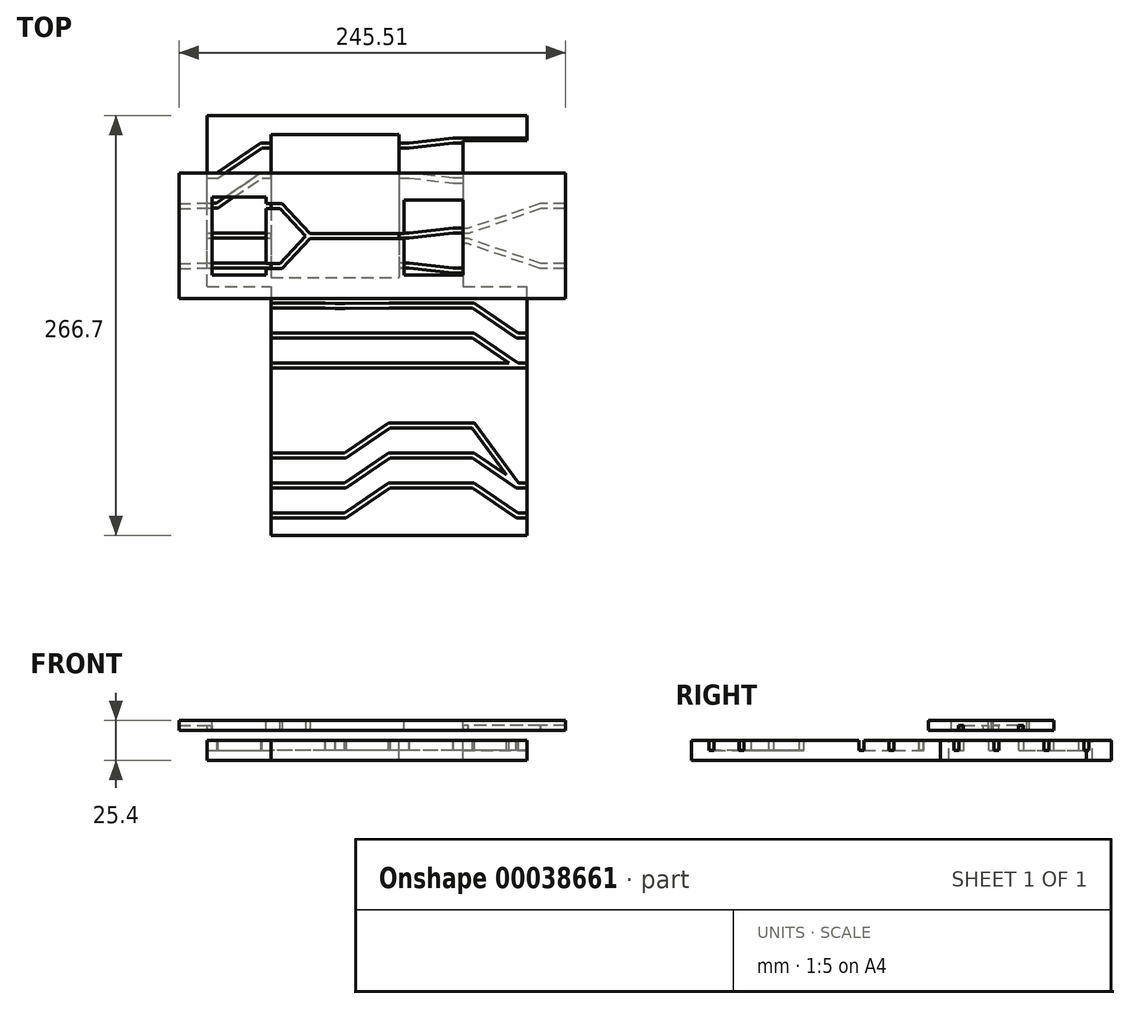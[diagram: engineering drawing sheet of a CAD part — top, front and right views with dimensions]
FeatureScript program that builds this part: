
annotation { "Feature Type Name" : "Feature", "Feature Type Description" : "" }
export const myFeature = defineFeature(function(context is Context, id is Id, definition is map)
    precondition{}
    {
        {
            var Q0;
            Q0=qCreatedBy(makeId("Top.planeOp"),FACE);
            var sketch = newSketch(context, id + "F0", { "sketchPlane" : qUnion([Q0])});
            skLineSegment(sketch, "E0.rect.bottom", {"start": v(-101.6, -133.35) * mm, "end": v(101.6, -133.35) * mm});
            skLineSegment(sketch, "E0.rect.top", {"start": v(-101.6, 133.35) * mm, "end": v(101.6, 133.35) * mm});
            skLineSegment(sketch, "E0.rect.left", {"start": v(-101.6, -133.35) * mm, "end": v(-101.6, 133.35) * mm});
            skLineSegment(sketch, "E0.rect.right", {"start": v(101.6, -133.35) * mm, "end": v(101.6, 133.35) * mm});
            skPoint(sketch, "E0.rect.middle", {"position": v(0, 0) * mm});
            skSolve(sketch);
        }
        {
            var Q0;
            Q0 = qSketchRegion(id + "F0", true);
            extrude(context, id + "F1", {"entities" : qUnion([Q0]), "depth" : 12.7 * mm});
        }
        {
            var Q0;
            Q0=makeQuery(id+"F1.opExtrude","CAP_FACE",FACE,{"disambiguationData":[OSD([sQuery(id+"F0.wireOp",EDGE,"E0.rect.bottom"),sQuery(id+"F0.wireOp",EDGE,"E0.rect.top"),sQuery(id+"F0.wireOp",EDGE,"E0.rect.left"),sQuery(id+"F0.wireOp",EDGE,"E0.rect.right")])],"isStart":false});
            var sketch = newSketch(context, id + "F2", { "sketchPlane" : qUnion([Q0])});
            skLineSegment(sketch, "E1", {"start": v(-101.6, 114.3) * mm, "end": v(101.6, 114.3) * mm, "construction": true});
            skLineSegment(sketch, "E2", {"start": v(-101.6, 95.25) * mm, "end": v(101.6, 95.25) * mm, "construction": true});
            skLineSegment(sketch, "E3", {"start": v(-101.6, 76.2) * mm, "end": v(101.6, 76.2) * mm, "construction": true});
            skLineSegment(sketch, "E4", {"start": v(-101.6, 57.15) * mm, "end": v(101.6, 57.15) * mm, "construction": true});
            skLineSegment(sketch, "E5", {"start": v(-101.6, 38.1) * mm, "end": v(101.6, 38.1) * mm, "construction": true});
            skLineSegment(sketch, "E6", {"start": v(-101.6, 12.69) * mm, "end": v(101.6, 12.69) * mm, "construction": true});
            skLineSegment(sketch, "E7", {"start": v(-101.6, -6.36) * mm, "end": v(101.6, -6.36) * mm, "construction": true});
            skLineSegment(sketch, "E8", {"start": v(-101.6, -25.41) * mm, "end": v(101.6, -25.41) * mm, "construction": true});
            skLineSegment(sketch, "E9", {"start": v(-101.6, -44.46) * mm, "end": v(101.6, -44.46) * mm, "construction": true});
            skLineSegment(sketch, "E10", {"start": v(-101.6, -63.51) * mm, "end": v(101.6, -63.51) * mm, "construction": true});
            skLineSegment(sketch, "E11", {"start": v(-101.6, -82.56) * mm, "end": v(101.6, -82.56) * mm, "construction": true});
            skLineSegment(sketch, "E12", {"start": v(-101.6, -101.61) * mm, "end": v(101.6, -101.61) * mm, "construction": true});
            skLineSegment(sketch, "E13", {"start": v(-101.6, -120.66) * mm, "end": v(101.6, -120.66) * mm, "construction": true});
            skLineSegment(sketch, "E14.0", {"start": v(-101.6, 133.35) * mm, "end": v(101.6, 133.35) * mm});
            skLineSegment(sketch, "E15.0", {"start": v(-101.6, -133.35) * mm, "end": v(-101.6, 133.35) * mm});
            skLineSegment(sketch, "E16.0", {"start": v(101.6, -133.35) * mm, "end": v(101.6, 133.35) * mm});
            skLineSegment(sketch, "E17.0", {"start": v(-101.6, -133.35) * mm, "end": v(101.6, -133.35) * mm});
            skLineSegment(sketch, "E18", {"start": v(-60.96, 133.35) * mm, "end": v(-60.96, -133.35) * mm, "construction": true});
            skLineSegment(sketch, "E19", {"start": v(-20.32, 133.35) * mm, "end": v(-20.32, -133.35) * mm, "construction": true});
            skLineSegment(sketch, "E20", {"start": v(20.32, -133.35) * mm, "end": v(20.32, 133.35) * mm, "construction": true});
            skLineSegment(sketch, "E21", {"start": v(60.96, 133.35) * mm, "end": v(60.96, -133.35) * mm, "construction": true});
            skLineSegment(sketch, "E22.0", {"start": v(-95.25, -133.35) * mm, "end": v(-95.25, 133.35) * mm, "construction": true});
            skLineSegment(sketch, "E23.0", {"start": v(-67.31, 133.35) * mm, "end": v(-67.31, -133.35) * mm, "construction": true});
            skLineSegment(sketch, "E24.0", {"start": v(-54.61, 133.35) * mm, "end": v(-54.61, -133.35) * mm, "construction": true});
            skLineSegment(sketch, "E25.0", {"start": v(-26.67, 133.35) * mm, "end": v(-26.67, -133.35) * mm, "construction": true});
            skLineSegment(sketch, "E26.0", {"start": v(-13.97, 133.35) * mm, "end": v(-13.97, -133.35) * mm, "construction": true});
            skLineSegment(sketch, "E27.0", {"start": v(26.67, -133.35) * mm, "end": v(26.67, 133.35) * mm, "construction": true});
            skLineSegment(sketch, "E28.0", {"start": v(13.97, -133.35) * mm, "end": v(13.97, 133.35) * mm, "construction": true});
            skLineSegment(sketch, "E29.0", {"start": v(54.6, 133.35) * mm, "end": v(54.6, -133.35) * mm, "construction": true});
            skLineSegment(sketch, "E30.0", {"start": v(67.3, 133.35) * mm, "end": v(67.3, -133.35) * mm, "construction": true});
            skLineSegment(sketch, "E31.0", {"start": v(95.25, -133.35) * mm, "end": v(95.25, 133.35) * mm, "construction": true});
            skLineSegment(sketch, "E32", {"start": v(-101.6, 95.25) * mm, "end": v(-95.25, 95.25) * mm});
            skLineSegment(sketch, "E33", {"start": v(-95.25, 95.25) * mm, "end": v(-67.31, 114.3) * mm});
            skLineSegment(sketch, "E34", {"start": v(-67.31, 114.3) * mm, "end": v(-60.96, 114.3) * mm});
            skLineSegment(sketch, "E35", {"start": v(-101.6, 76.2) * mm, "end": v(-95.25, 76.2) * mm});
            skLineSegment(sketch, "E36", {"start": v(-95.25, 76.2) * mm, "end": v(-67.31, 95.25) * mm});
            skLineSegment(sketch, "E37", {"start": v(-67.31, 95.25) * mm, "end": v(-60.96, 95.25) * mm});
            skLineSegment(sketch, "E38", {"start": v(-101.6, 57.15) * mm, "end": v(-95.25, 57.15) * mm});
            skLineSegment(sketch, "E39", {"start": v(-95.25, 57.15) * mm, "end": v(-67.31, 57.15) * mm});
            skLineSegment(sketch, "E40", {"start": v(-67.31, 57.15) * mm, "end": v(-60.96, 57.15) * mm});
            skLineSegment(sketch, "E41", {"start": v(-101.6, 38.1) * mm, "end": v(-95.25, 38.1) * mm});
            skLineSegment(sketch, "E42", {"start": v(-95.25, 38.1) * mm, "end": v(-67.31, 38.1) * mm});
            skLineSegment(sketch, "E43", {"start": v(-67.31, 38.1) * mm, "end": v(-60.96, 38.1) * mm});
            skLineSegment(sketch, "E44.bottom", {"start": v(-60.96, 121.3) * mm, "end": v(-20.32, 121.3) * mm});
            skLineSegment(sketch, "E44.top", {"start": v(-60.96, 30.34) * mm, "end": v(-20.32, 30.34) * mm});
            skLineSegment(sketch, "E44.left", {"start": v(-60.96, 121.3) * mm, "end": v(-60.96, 30.34) * mm});
            skLineSegment(sketch, "E44.right", {"start": v(-20.32, 121.3) * mm, "end": v(-20.32, 30.34) * mm});
            skLineSegment(sketch, "E45.bottom", {"start": v(60.96, 133.35) * mm, "end": v(101.6, 133.35) * mm});
            skLineSegment(sketch, "E45.top", {"start": v(60.96, 24.81) * mm, "end": v(101.6, 24.81) * mm});
            skLineSegment(sketch, "E45.left", {"start": v(60.96, 133.35) * mm, "end": v(60.96, 24.81) * mm});
            skLineSegment(sketch, "E45.right", {"start": v(101.6, 133.35) * mm, "end": v(101.6, 24.81) * mm});
            skLineSegment(sketch, "E46.bottom", {"start": v(-101.6, 24.81) * mm, "end": v(-60.96, 24.81) * mm});
            skLineSegment(sketch, "E46.top", {"start": v(-101.6, -133.35) * mm, "end": v(-60.96, -133.35) * mm});
            skLineSegment(sketch, "E46.left", {"start": v(-101.6, 24.81) * mm, "end": v(-101.6, -133.35) * mm});
            skLineSegment(sketch, "E46.right", {"start": v(-60.96, 24.81) * mm, "end": v(-60.96, -133.35) * mm});
            skLineSegment(sketch, "E47", {"start": v(-60.96, 12.69) * mm, "end": v(-54.61, 12.69) * mm});
            skLineSegment(sketch, "E48", {"start": v(-54.61, 12.69) * mm, "end": v(-26.67, 12.69) * mm});
            skLineSegment(sketch, "E49", {"start": v(-26.67, 12.69) * mm, "end": v(-20.47, 12.5) * mm});
            skLineSegment(sketch, "E50", {"start": v(-20.47, 12.5) * mm, "end": v(-13.97, 12.5) * mm});
            skLineSegment(sketch, "E51", {"start": v(-13.97, 12.5) * mm, "end": v(13.97, 12.69) * mm});
            skLineSegment(sketch, "E52", {"start": v(13.97, 12.69) * mm, "end": v(20.69, 12.68) * mm});
            skLineSegment(sketch, "E53", {"start": v(20.69, 12.68) * mm, "end": v(26.67, 12.68) * mm});
            skLineSegment(sketch, "E54", {"start": v(26.67, 12.68) * mm, "end": v(54.6, 12.68) * mm});
            skLineSegment(sketch, "E55", {"start": v(54.6, 12.68) * mm, "end": v(60.96, 12.68) * mm});
            skLineSegment(sketch, "E56", {"start": v(60.96, 12.68) * mm, "end": v(67.3, 12.68) * mm});
            skLineSegment(sketch, "E57", {"start": v(67.3, 12.68) * mm, "end": v(95.25, -6.36) * mm});
            skLineSegment(sketch, "E58", {"start": v(95.25, -6.36) * mm, "end": v(101.6, -6.36) * mm});
            skLineSegment(sketch, "E59", {"start": v(-60.96, -6.36) * mm, "end": v(-54.61, -6.36) * mm});
            skLineSegment(sketch, "E60", {"start": v(-54.61, -6.36) * mm, "end": v(-26.67, -6.36) * mm});
            skLineSegment(sketch, "E61", {"start": v(-26.67, -6.36) * mm, "end": v(-20.32, -6.36) * mm});
            skLineSegment(sketch, "E62", {"start": v(-20.32, -6.36) * mm, "end": v(-13.97, -6.36) * mm});
            skLineSegment(sketch, "E63", {"start": v(-13.97, -6.36) * mm, "end": v(13.97, -6.36) * mm});
            skLineSegment(sketch, "E64", {"start": v(13.97, -6.36) * mm, "end": v(20.32, -6.36) * mm});
            skLineSegment(sketch, "E65", {"start": v(20.32, -6.36) * mm, "end": v(26.67, -6.36) * mm});
            skLineSegment(sketch, "E66", {"start": v(26.67, -6.36) * mm, "end": v(54.6, -6.36) * mm});
            skLineSegment(sketch, "E67", {"start": v(54.6, -6.36) * mm, "end": v(60.96, -6.36) * mm});
            skLineSegment(sketch, "E68", {"start": v(60.96, -6.36) * mm, "end": v(67.3, -6.36) * mm});
            skLineSegment(sketch, "E69", {"start": v(67.3, -6.36) * mm, "end": v(95.25, -25.41) * mm});
            skLineSegment(sketch, "E70", {"start": v(95.25, -25.41) * mm, "end": v(101.6, -25.41) * mm});
            skLineSegment(sketch, "E71", {"start": v(-60.96, -25.41) * mm, "end": v(-54.61, -25.41) * mm});
            skLineSegment(sketch, "E72", {"start": v(-54.61, -25.41) * mm, "end": v(-26.67, -25.41) * mm});
            skLineSegment(sketch, "E73", {"start": v(-26.67, -25.41) * mm, "end": v(-20.32, -25.41) * mm});
            skLineSegment(sketch, "E74", {"start": v(-20.32, -25.41) * mm, "end": v(-13.97, -25.41) * mm});
            skLineSegment(sketch, "E75", {"start": v(-13.97, -25.41) * mm, "end": v(13.97, -25.41) * mm});
            skLineSegment(sketch, "E76", {"start": v(13.97, -25.41) * mm, "end": v(20.32, -25.41) * mm});
            skLineSegment(sketch, "E77", {"start": v(20.32, -25.41) * mm, "end": v(26.67, -25.41) * mm});
            skLineSegment(sketch, "E78", {"start": v(26.67, -25.41) * mm, "end": v(54.6, -25.41) * mm});
            skLineSegment(sketch, "E79", {"start": v(54.6, -25.41) * mm, "end": v(60.96, -25.41) * mm});
            skLineSegment(sketch, "E80", {"start": v(60.96, -25.41) * mm, "end": v(67.3, -25.41) * mm});
            skLineSegment(sketch, "E81", {"start": v(67.3, -25.41) * mm, "end": v(95.25, -25.41) * mm});
            skLineSegment(sketch, "E82", {"start": v(-60.96, -82.56) * mm, "end": v(-54.61, -82.56) * mm});
            skLineSegment(sketch, "E83", {"start": v(-54.61, -82.56) * mm, "end": v(-26.67, -82.56) * mm});
            skLineSegment(sketch, "E84", {"start": v(-26.67, -82.56) * mm, "end": v(-20.32, -82.56) * mm});
            skLineSegment(sketch, "E85", {"start": v(-20.32, -82.56) * mm, "end": v(-13.97, -82.56) * mm});
            skLineSegment(sketch, "E86", {"start": v(-13.97, -82.56) * mm, "end": v(13.97, -63.51) * mm});
            skLineSegment(sketch, "E87", {"start": v(13.97, -63.51) * mm, "end": v(20.32, -63.51) * mm});
            skLineSegment(sketch, "E88", {"start": v(20.32, -63.51) * mm, "end": v(26.67, -63.51) * mm});
            skLineSegment(sketch, "E89", {"start": v(26.67, -63.51) * mm, "end": v(54.6, -63.51) * mm});
            skLineSegment(sketch, "E90", {"start": v(54.6, -63.51) * mm, "end": v(60.96, -63.51) * mm});
            skLineSegment(sketch, "E91", {"start": v(60.96, -63.51) * mm, "end": v(67.3, -63.51) * mm});
            skLineSegment(sketch, "E92", {"start": v(67.3, -63.51) * mm, "end": v(95.25, -101.61) * mm});
            skLineSegment(sketch, "E93", {"start": v(95.25, -101.61) * mm, "end": v(101.6, -101.61) * mm});
            skLineSegment(sketch, "E94", {"start": v(-60.96, -101.61) * mm, "end": v(-54.61, -101.61) * mm});
            skLineSegment(sketch, "E95", {"start": v(-54.61, -101.61) * mm, "end": v(-26.67, -101.61) * mm});
            skLineSegment(sketch, "E96", {"start": v(-26.67, -101.61) * mm, "end": v(-20.32, -101.61) * mm});
            skLineSegment(sketch, "E97", {"start": v(-20.32, -101.61) * mm, "end": v(-13.97, -101.61) * mm});
            skLineSegment(sketch, "E98", {"start": v(-13.97, -101.61) * mm, "end": v(13.97, -82.56) * mm});
            skLineSegment(sketch, "E99", {"start": v(13.97, -82.56) * mm, "end": v(20.32, -82.56) * mm});
            skLineSegment(sketch, "E100", {"start": v(20.32, -82.56) * mm, "end": v(26.67, -82.56) * mm});
            skLineSegment(sketch, "E101", {"start": v(26.67, -82.56) * mm, "end": v(54.6, -82.56) * mm});
            skLineSegment(sketch, "E102", {"start": v(54.6, -82.56) * mm, "end": v(60.96, -82.56) * mm});
            skLineSegment(sketch, "E103", {"start": v(60.96, -82.56) * mm, "end": v(67.3, -82.56) * mm});
            skLineSegment(sketch, "E104", {"start": v(67.3, -82.56) * mm, "end": v(95.25, -101.61) * mm});
            skLineSegment(sketch, "E105", {"start": v(-60.96, -120.66) * mm, "end": v(-54.61, -120.66) * mm});
            skLineSegment(sketch, "E106", {"start": v(-54.61, -120.66) * mm, "end": v(-26.67, -120.66) * mm});
            skLineSegment(sketch, "E107", {"start": v(-26.67, -120.66) * mm, "end": v(-20.32, -120.66) * mm});
            skLineSegment(sketch, "E108", {"start": v(-20.32, -120.66) * mm, "end": v(-13.97, -120.66) * mm});
            skLineSegment(sketch, "E109", {"start": v(-13.97, -120.66) * mm, "end": v(13.97, -101.61) * mm});
            skLineSegment(sketch, "E110", {"start": v(13.97, -101.61) * mm, "end": v(20.32, -101.61) * mm});
            skLineSegment(sketch, "E111", {"start": v(20.32, -101.61) * mm, "end": v(26.67, -101.61) * mm});
            skLineSegment(sketch, "E112", {"start": v(26.67, -101.61) * mm, "end": v(54.6, -101.61) * mm});
            skLineSegment(sketch, "E113", {"start": v(54.6, -101.61) * mm, "end": v(60.96, -101.61) * mm});
            skLineSegment(sketch, "E114", {"start": v(60.96, -101.61) * mm, "end": v(67.3, -101.61) * mm});
            skLineSegment(sketch, "E115", {"start": v(67.3, -101.61) * mm, "end": v(95.25, -120.66) * mm});
            skLineSegment(sketch, "E116", {"start": v(95.25, -120.66) * mm, "end": v(101.6, -120.66) * mm});
            skLineSegment(sketch, "E117.0", {"start": v(-101.6, 117.47) * mm, "end": v(101.6, 117.48) * mm, "construction": true});
            skLineSegment(sketch, "E118.0", {"start": v(-101.6, 92.07) * mm, "end": v(101.6, 92.08) * mm, "construction": true});
            skLineSegment(sketch, "E119.0", {"start": v(-101.6, 60.32) * mm, "end": v(101.6, 60.33) * mm, "construction": true});
            skLineSegment(sketch, "E120", {"start": v(20.32, 114.3) * mm, "end": v(26.67, 114.3) * mm});
            skLineSegment(sketch, "E121", {"start": v(26.67, 114.3) * mm, "end": v(54.6, 117.48) * mm});
            skLineSegment(sketch, "E122", {"start": v(54.6, 117.48) * mm, "end": v(60.96, 117.48) * mm});
            skLineSegment(sketch, "E123", {"start": v(20.32, 95.25) * mm, "end": v(26.67, 95.25) * mm});
            skLineSegment(sketch, "E124", {"start": v(26.67, 95.25) * mm, "end": v(54.6, 92.08) * mm});
            skLineSegment(sketch, "E125", {"start": v(54.6, 92.08) * mm, "end": v(60.96, 92.08) * mm});
            skLineSegment(sketch, "E126.0", {"start": v(-101.6, 34.92) * mm, "end": v(101.6, 34.93) * mm, "construction": true});
            skLineSegment(sketch, "E127", {"start": v(20.32, 57.15) * mm, "end": v(26.67, 57.15) * mm});
            skLineSegment(sketch, "E128", {"start": v(26.67, 57.15) * mm, "end": v(54.6, 60.32) * mm});
            skLineSegment(sketch, "E129", {"start": v(54.6, 60.32) * mm, "end": v(60.96, 60.32) * mm});
            skLineSegment(sketch, "E130", {"start": v(20.32, 38.1) * mm, "end": v(26.67, 38.1) * mm});
            skLineSegment(sketch, "E131", {"start": v(26.67, 38.1) * mm, "end": v(54.6, 34.93) * mm});
            skLineSegment(sketch, "E132", {"start": v(54.6, 34.92) * mm, "end": v(60.96, 34.93) * mm});
            skLineSegment(sketch, "E133", {"start": v(60.96, 117.48) * mm, "end": v(67.3, 117.48) * mm});
            skLineSegment(sketch, "E134", {"start": v(67.3, 117.48) * mm, "end": v(95.25, 117.48) * mm});
            skLineSegment(sketch, "E135", {"start": v(95.25, 117.48) * mm, "end": v(101.6, 117.48) * mm});
            skLineSegment(sketch, "E136", {"start": v(60.96, 92.08) * mm, "end": v(67.3, 92.08) * mm});
            skLineSegment(sketch, "E137", {"start": v(67.3, 92.08) * mm, "end": v(95.25, 92.08) * mm});
            skLineSegment(sketch, "E138", {"start": v(95.25, 92.08) * mm, "end": v(101.6, 92.08) * mm});
            skLineSegment(sketch, "E139", {"start": v(60.96, 60.32) * mm, "end": v(67.3, 60.32) * mm});
            skLineSegment(sketch, "E140", {"start": v(67.3, 60.32) * mm, "end": v(95.25, 60.32) * mm});
            skLineSegment(sketch, "E141", {"start": v(95.25, 60.33) * mm, "end": v(101.6, 60.33) * mm});
            skLineSegment(sketch, "E142", {"start": v(60.96, 34.93) * mm, "end": v(67.3, 34.93) * mm});
            skLineSegment(sketch, "E143", {"start": v(67.3, 34.93) * mm, "end": v(95.25, 34.93) * mm});
            skLineSegment(sketch, "E144", {"start": v(95.25, 34.93) * mm, "end": v(101.6, 34.93) * mm});
            skLineSegment(sketch, "E145.bottom", {"start": v(-20.32, 121.3) * mm, "end": v(20.32, 121.3) * mm});
            skLineSegment(sketch, "E145.top", {"start": v(-20.32, 30.34) * mm, "end": v(20.32, 30.34) * mm});
            skLineSegment(sketch, "E145.right", {"start": v(20.32, 121.3) * mm, "end": v(20.32, 30.34) * mm});
            skSolve(sketch);
        }
        {
            var Q0;
            {var subQ4=sQuery(id+"F2.wireOp",EDGE,"E44.bottom");Q0=makeQuery(id+"F2.imprint","IMPRINT",FACE,{"disambiguationData":[TD([[makeQuery(id+"F2.imprint","IMPRINT",EDGE,{"derivedFrom":subQ4}),-1.0]])]});}
            var Q1;
            {var subQ6=sQuery(id+"F2.wireOp",EDGE,"E46.bottom");Q1=makeQuery(id+"F2.imprint","IMPRINT",FACE,{"disambiguationData":[TD([[makeQuery(id+"F2.imprint","IMPRINT",EDGE,{"derivedFrom":subQ6}),-1.0]])]});}
            var Q2;
            Q2=makeQuery(id+"F2.imprint","IMPRINT",FACE,{"disambiguationData":[TD([[makeQuery(id+"F2.imprint","IMPRINT",EDGE,{"derivedFrom":sQuery(id+"F2.wireOp",EDGE,"E45.bottom")}),-1.0]])]});
            var Q3;
            {var subQ4=sQuery(id+"F2.wireOp",EDGE,"E133");Q3=makeQuery(id+"F2.imprint","IMPRINT",FACE,{"disambiguationData":[TD([[makeQuery(id+"F2.imprint","IMPRINT",EDGE,{"derivedFrom":subQ4}),-1.0]])]});}
            var Q4;
            {var subQ5=sQuery(id+"F2.wireOp",EDGE,"E136");Q4=makeQuery(id+"F2.imprint","IMPRINT",FACE,{"disambiguationData":[TD([[makeQuery(id+"F2.imprint","IMPRINT",EDGE,{"derivedFrom":subQ5}),-1.0]])]});}
            var Q5;
            {var subQ4=sQuery(id+"F2.wireOp",EDGE,"E139");Q5=makeQuery(id+"F2.imprint","IMPRINT",FACE,{"disambiguationData":[TD([[makeQuery(id+"F2.imprint","IMPRINT",EDGE,{"derivedFrom":subQ4}),-1.0]])]});}
            var Q6;
            {var subQ1=sQuery(id+"F2.wireOp",EDGE,"E45.top");Q6=makeQuery(id+"F2.imprint","IMPRINT",FACE,{"disambiguationData":[TD([[makeQuery(id+"F2.imprint","IMPRINT",EDGE,{"derivedFrom":subQ1}),1.0]])]});}
            var Q7;
            {var subQ6=sQuery(id+"F2.wireOp",EDGE,"E145.bottom");Q7=makeQuery(id+"F2.imprint","IMPRINT",FACE,{"disambiguationData":[TD([[makeQuery(id+"F2.imprint","IMPRINT",EDGE,{"derivedFrom":subQ6}),-1.0]])]});}
            extrude(context, id + "F3", {"entities" : qUnion([Q0, Q1, Q2, Q3, Q4, Q5, Q6, Q7]), "operationType" : NewBodyOperationType.REMOVE, "oppositeDirection" : true, "depth" : 25.4 * mm});
        }
        {
            var Q0;
            Q0=makeQuery(id+"F1.opExtrude","SWEPT_FACE",FACE,{"disambiguationData":[OSD([sQuery(id+"F0.wireOp",EDGE,"E0.rect.right")])]});
            var sketch = newSketch(context, id + "F4", { "sketchPlane" : qUnion([Q0])});
            skPoint(sketch, "E146.0", {"position": v(-120.66, 12.7) * mm});
            skPoint(sketch, "E147.0", {"position": v(-101.61, 12.7) * mm});
            skPoint(sketch, "E148.0", {"position": v(-25.41, 12.7) * mm});
            skPoint(sketch, "E149.0", {"position": v(-6.36, 12.7) * mm});
            skPoint(sketch, "E150.0", {"position": v(34.92, 12.7) * mm});
            skPoint(sketch, "E151.0", {"position": v(60.32, 12.7) * mm});
            skPoint(sketch, "E152.0", {"position": v(92.08, 12.7) * mm});
            skPoint(sketch, "E153.0", {"position": v(117.48, 12.7) * mm});
            skLineSegment(sketch, "E154", {"start": v(-133.35, 6.35) * mm, "end": v(123.8, 6.35) * mm, "construction": true});
            skLineSegment(sketch, "E155.rect.bottom", {"start": v(-119.08, 6.35) * mm, "end": v(-122.25, 6.35) * mm});
            skLineSegment(sketch, "E155.rect.top", {"start": v(-119.08, 19.05) * mm, "end": v(-122.25, 19.05) * mm});
            skLineSegment(sketch, "E155.rect.left", {"start": v(-119.08, 6.35) * mm, "end": v(-119.08, 19.05) * mm});
            skLineSegment(sketch, "E155.rect.right", {"start": v(-122.25, 6.35) * mm, "end": v(-122.25, 19.05) * mm});
            skLineSegment(sketch, "E156.rect.bottom", {"start": v(-100.03, 6.35) * mm, "end": v(-103.2, 6.35) * mm});
            skLineSegment(sketch, "E156.rect.top", {"start": v(-100.03, 19.05) * mm, "end": v(-103.2, 19.05) * mm});
            skLineSegment(sketch, "E156.rect.left", {"start": v(-100.03, 6.35) * mm, "end": v(-100.03, 19.05) * mm});
            skLineSegment(sketch, "E156.rect.right", {"start": v(-103.2, 6.35) * mm, "end": v(-103.2, 19.05) * mm});
            skLineSegment(sketch, "E157.rect.bottom", {"start": v(-23.83, 6.35) * mm, "end": v(-27, 6.35) * mm});
            skLineSegment(sketch, "E157.rect.top", {"start": v(-23.83, 19.05) * mm, "end": v(-27, 19.05) * mm});
            skLineSegment(sketch, "E157.rect.left", {"start": v(-23.83, 6.35) * mm, "end": v(-23.83, 19.05) * mm});
            skLineSegment(sketch, "E157.rect.right", {"start": v(-27, 6.35) * mm, "end": v(-27, 19.05) * mm});
            skLineSegment(sketch, "E158.rect.bottom", {"start": v(-4.78, 6.35) * mm, "end": v(-7.95, 6.35) * mm});
            skLineSegment(sketch, "E158.rect.top", {"start": v(-4.78, 19.05) * mm, "end": v(-7.95, 19.05) * mm});
            skLineSegment(sketch, "E158.rect.left", {"start": v(-4.78, 6.35) * mm, "end": v(-4.78, 19.05) * mm});
            skLineSegment(sketch, "E158.rect.right", {"start": v(-7.95, 6.35) * mm, "end": v(-7.95, 19.05) * mm});
            skLineSegment(sketch, "E159.rect.bottom", {"start": v(36.51, 6.35) * mm, "end": v(33.34, 6.35) * mm});
            skLineSegment(sketch, "E159.rect.top", {"start": v(36.51, 19.05) * mm, "end": v(33.34, 19.05) * mm});
            skLineSegment(sketch, "E159.rect.left", {"start": v(36.51, 6.35) * mm, "end": v(36.51, 19.05) * mm});
            skLineSegment(sketch, "E159.rect.right", {"start": v(33.34, 6.35) * mm, "end": v(33.34, 19.05) * mm});
            skLineSegment(sketch, "E160.rect.bottom", {"start": v(61.91, 6.35) * mm, "end": v(58.74, 6.35) * mm});
            skLineSegment(sketch, "E160.rect.top", {"start": v(61.91, 19.05) * mm, "end": v(58.74, 19.05) * mm});
            skLineSegment(sketch, "E160.rect.left", {"start": v(61.91, 6.35) * mm, "end": v(61.91, 19.05) * mm});
            skLineSegment(sketch, "E160.rect.right", {"start": v(58.74, 6.35) * mm, "end": v(58.74, 19.05) * mm});
            skLineSegment(sketch, "E161.rect.bottom", {"start": v(93.66, 6.35) * mm, "end": v(90.49, 6.35) * mm});
            skLineSegment(sketch, "E161.rect.top", {"start": v(93.66, 19.05) * mm, "end": v(90.49, 19.05) * mm});
            skLineSegment(sketch, "E161.rect.left", {"start": v(93.66, 6.35) * mm, "end": v(93.66, 19.05) * mm});
            skLineSegment(sketch, "E161.rect.right", {"start": v(90.49, 6.35) * mm, "end": v(90.49, 19.05) * mm});
            skLineSegment(sketch, "E162.rect.bottom", {"start": v(119.06, 6.35) * mm, "end": v(115.89, 6.35) * mm});
            skLineSegment(sketch, "E162.rect.top", {"start": v(119.06, 19.05) * mm, "end": v(115.89, 19.05) * mm});
            skLineSegment(sketch, "E162.rect.left", {"start": v(119.06, 6.35) * mm, "end": v(119.06, 19.05) * mm});
            skLineSegment(sketch, "E162.rect.right", {"start": v(115.89, 6.35) * mm, "end": v(115.89, 19.05) * mm});
            skSolve(sketch);
        }
        {
            var Q0;
            {var subQ5=sQuery(id+"F4.wireOp",EDGE,"E155.rect.bottom");Q0=makeQuery(id+"F4.imprint","IMPRINT",FACE,{"disambiguationData":[TD([[makeQuery(id+"F4.imprint","IMPRINT",EDGE,{"derivedFrom":subQ5}),-1.0]])]});}
            var Q1;
            Q1=sQuery(id+"F2.wireOp",EDGE,"E116");
            var Q2;
            Q2=sQuery(id+"F2.wireOp",EDGE,"E115");
            var Q3;
            Q3=sQuery(id+"F2.wireOp",EDGE,"E114");
            var Q4;
            Q4=sQuery(id+"F2.wireOp",EDGE,"E113");
            var Q5;
            Q5=sQuery(id+"F2.wireOp",EDGE,"E112");
            var Q6;
            Q6=sQuery(id+"F2.wireOp",EDGE,"E111");
            var Q7;
            Q7=sQuery(id+"F2.wireOp",EDGE,"E110");
            var Q8;
            Q8=sQuery(id+"F2.wireOp",EDGE,"E109");
            var Q9;
            Q9=sQuery(id+"F2.wireOp",EDGE,"E108");
            var Q10;
            Q10=sQuery(id+"F2.wireOp",EDGE,"E107");
            var Q11;
            Q11=sQuery(id+"F2.wireOp",EDGE,"E106");
            var Q12;
            Q12=sQuery(id+"F2.wireOp",EDGE,"E105");
            sweep(context, id + "F5", {"operationType" : NewBodyOperationType.REMOVE, "profiles" : qUnion([Q0]), "path" : qUnion([Q1, Q2, Q3, Q4, Q5, Q6, Q7, Q8, Q9, Q10, Q11, Q12])});
        }
        {
            var Q0;
            {var subQ5=sQuery(id+"F4.wireOp",EDGE,"E156.rect.bottom");Q0=makeQuery(id+"F4.imprint","IMPRINT",FACE,{"disambiguationData":[TD([[makeQuery(id+"F4.imprint","IMPRINT",EDGE,{"derivedFrom":subQ5}),-1.0]])]});}
            var Q1;
            Q1=sQuery(id+"F2.wireOp",EDGE,"E93");
            var Q2;
            Q2=sQuery(id+"F2.wireOp",EDGE,"E104");
            var Q3;
            Q3=sQuery(id+"F2.wireOp",EDGE,"E103");
            var Q4;
            Q4=sQuery(id+"F2.wireOp",EDGE,"E102");
            var Q5;
            Q5=sQuery(id+"F2.wireOp",EDGE,"E101");
            var Q6;
            Q6=sQuery(id+"F2.wireOp",EDGE,"E100");
            var Q7;
            Q7=sQuery(id+"F2.wireOp",EDGE,"E99");
            var Q8;
            Q8=sQuery(id+"F2.wireOp",EDGE,"E98");
            var Q9;
            Q9=sQuery(id+"F2.wireOp",EDGE,"E97");
            var Q10;
            Q10=sQuery(id+"F2.wireOp",EDGE,"E96");
            var Q11;
            Q11=sQuery(id+"F2.wireOp",EDGE,"E95");
            var Q12;
            Q12=sQuery(id+"F2.wireOp",EDGE,"E94");
            sweep(context, id + "F6", {"operationType" : NewBodyOperationType.REMOVE, "profiles" : qUnion([Q0]), "path" : qUnion([Q1, Q2, Q3, Q4, Q5, Q6, Q7, Q8, Q9, Q10, Q11, Q12])});
        }
        {
            var Q0;
            {var subQ5=sQuery(id+"F4.wireOp",EDGE,"E156.rect.bottom");Q0=makeQuery(id+"F4.imprint","IMPRINT",FACE,{"disambiguationData":[TD([[makeQuery(id+"F4.imprint","IMPRINT",EDGE,{"derivedFrom":subQ5}),-1.0]])]});}
            var Q1;
            Q1=sQuery(id+"F2.wireOp",EDGE,"E93");
            var Q2;
            Q2=sQuery(id+"F2.wireOp",EDGE,"E92");
            var Q3;
            Q3=sQuery(id+"F2.wireOp",EDGE,"E91");
            var Q4;
            Q4=sQuery(id+"F2.wireOp",EDGE,"E90");
            var Q5;
            Q5=sQuery(id+"F2.wireOp",EDGE,"E89");
            var Q6;
            Q6=sQuery(id+"F2.wireOp",EDGE,"E88");
            var Q7;
            Q7=sQuery(id+"F2.wireOp",EDGE,"E87");
            var Q8;
            Q8=sQuery(id+"F2.wireOp",EDGE,"E86");
            var Q9;
            Q9=sQuery(id+"F2.wireOp",EDGE,"E85");
            var Q10;
            Q10=sQuery(id+"F2.wireOp",EDGE,"E84");
            var Q11;
            Q11=sQuery(id+"F2.wireOp",EDGE,"E83");
            var Q12;
            Q12=sQuery(id+"F2.wireOp",EDGE,"E82");
            sweep(context, id + "F7", {"operationType" : NewBodyOperationType.REMOVE, "profiles" : qUnion([Q0]), "path" : qUnion([Q1, Q2, Q3, Q4, Q5, Q6, Q7, Q8, Q9, Q10, Q11, Q12])});
        }
        {
            var Q0;
            {var subQ5=sQuery(id+"F4.wireOp",EDGE,"E157.rect.bottom");Q0=makeQuery(id+"F4.imprint","IMPRINT",FACE,{"disambiguationData":[TD([[makeQuery(id+"F4.imprint","IMPRINT",EDGE,{"derivedFrom":subQ5}),-1.0]])]});}
            var Q1;
            Q1=sQuery(id+"F2.wireOp",EDGE,"E70");
            var Q2;
            Q2=sQuery(id+"F2.wireOp",EDGE,"E81");
            var Q3;
            Q3=sQuery(id+"F2.wireOp",EDGE,"E80");
            var Q4;
            Q4=sQuery(id+"F2.wireOp",EDGE,"E79");
            var Q5;
            Q5=sQuery(id+"F2.wireOp",EDGE,"E78");
            var Q6;
            Q6=sQuery(id+"F2.wireOp",EDGE,"E77");
            var Q7;
            Q7=sQuery(id+"F2.wireOp",EDGE,"E76");
            var Q8;
            Q8=sQuery(id+"F2.wireOp",EDGE,"E75");
            var Q9;
            Q9=sQuery(id+"F2.wireOp",EDGE,"E74");
            var Q10;
            Q10=sQuery(id+"F2.wireOp",EDGE,"E73");
            var Q11;
            Q11=sQuery(id+"F2.wireOp",EDGE,"E72");
            var Q12;
            Q12=sQuery(id+"F2.wireOp",EDGE,"E71");
            sweep(context, id + "F8", {"operationType" : NewBodyOperationType.REMOVE, "profiles" : qUnion([Q0]), "path" : qUnion([Q1, Q2, Q3, Q4, Q5, Q6, Q7, Q8, Q9, Q10, Q11, Q12])});
        }
        {
            var Q0;
            {var subQ5=sQuery(id+"F4.wireOp",EDGE,"E158.rect.bottom");Q0=makeQuery(id+"F4.imprint","IMPRINT",FACE,{"disambiguationData":[TD([[makeQuery(id+"F4.imprint","IMPRINT",EDGE,{"derivedFrom":subQ5}),-1.0]])]});}
            var Q1;
            Q1=sQuery(id+"F2.wireOp",EDGE,"E58");
            var Q2;
            Q2=sQuery(id+"F2.wireOp",EDGE,"E57");
            var Q3;
            Q3=sQuery(id+"F2.wireOp",EDGE,"E56");
            var Q4;
            Q4=sQuery(id+"F2.wireOp",EDGE,"E55");
            var Q5;
            Q5=sQuery(id+"F2.wireOp",EDGE,"E54");
            var Q6;
            Q6=sQuery(id+"F2.wireOp",EDGE,"E53");
            var Q7;
            Q7=sQuery(id+"F2.wireOp",EDGE,"E52");
            var Q8;
            Q8=sQuery(id+"F2.wireOp",EDGE,"E51");
            var Q9;
            Q9=sQuery(id+"F2.wireOp",EDGE,"E50");
            var Q10;
            Q10=sQuery(id+"F2.wireOp",EDGE,"E49");
            var Q11;
            Q11=sQuery(id+"F2.wireOp",EDGE,"E48");
            var Q12;
            Q12=sQuery(id+"F2.wireOp",EDGE,"E47");
            sweep(context, id + "F9", {"operationType" : NewBodyOperationType.REMOVE, "profiles" : qUnion([Q0]), "path" : qUnion([Q1, Q2, Q3, Q4, Q5, Q6, Q7, Q8, Q9, Q10, Q11, Q12])});
        }
        {
            var Q0;
            {var subQ5=sQuery(id+"F4.wireOp",EDGE,"E157.rect.bottom");Q0=makeQuery(id+"F4.imprint","IMPRINT",FACE,{"disambiguationData":[TD([[makeQuery(id+"F4.imprint","IMPRINT",EDGE,{"derivedFrom":subQ5}),-1.0]])]});}
            var Q1;
            Q1=sQuery(id+"F2.wireOp",EDGE,"E70");
            var Q2;
            Q2=sQuery(id+"F2.wireOp",EDGE,"E69");
            var Q3;
            Q3=sQuery(id+"F2.wireOp",EDGE,"E68");
            var Q4;
            Q4=sQuery(id+"F2.wireOp",EDGE,"E67");
            var Q5;
            Q5=sQuery(id+"F2.wireOp",EDGE,"E66");
            var Q6;
            Q6=sQuery(id+"F2.wireOp",EDGE,"E65");
            var Q7;
            Q7=sQuery(id+"F2.wireOp",EDGE,"E64");
            var Q8;
            Q8=sQuery(id+"F2.wireOp",EDGE,"E63");
            var Q9;
            Q9=sQuery(id+"F2.wireOp",EDGE,"E62");
            var Q10;
            Q10=sQuery(id+"F2.wireOp",EDGE,"E61");
            var Q11;
            Q11=sQuery(id+"F2.wireOp",EDGE,"E60");
            var Q12;
            Q12=sQuery(id+"F2.wireOp",EDGE,"E59");
            sweep(context, id + "F10", {"operationType" : NewBodyOperationType.REMOVE, "profiles" : qUnion([Q0]), "path" : qUnion([Q1, Q2, Q3, Q4, Q5, Q6, Q7, Q8, Q9, Q10, Q11, Q12])});
        }
        {
            var Q0;
            Q0=makeQuery(id+"F4.imprint","IMPRINT",FACE,{"disambiguationData":[TD([[makeQuery(id+"F4.imprint","IMPRINT",EDGE,{"derivedFrom":sQuery(id+"F4.wireOp",EDGE,"E159.rect.bottom")}),-1.0]])]});
            var Q1;
            Q1=sQuery(id+"F2.wireOp",EDGE,"E144");
            var Q2;
            Q2=sQuery(id+"F2.wireOp",EDGE,"E143");
            var Q3;
            Q3=sQuery(id+"F2.wireOp",EDGE,"E142");
            var Q4;
            Q4=sQuery(id+"F2.wireOp",EDGE,"E132");
            var Q5;
            Q5=sQuery(id+"F2.wireOp",EDGE,"E131");
            var Q6;
            Q6=sQuery(id+"F2.wireOp",EDGE,"E130");
            sweep(context, id + "F11", {"operationType" : NewBodyOperationType.REMOVE, "profiles" : qUnion([Q0]), "path" : qUnion([Q1, Q2, Q3, Q4, Q5, Q6])});
        }
        {
            var Q0;
            Q0=makeQuery(id+"F4.imprint","IMPRINT",FACE,{"disambiguationData":[TD([[makeQuery(id+"F4.imprint","IMPRINT",EDGE,{"derivedFrom":sQuery(id+"F4.wireOp",EDGE,"E160.rect.bottom")}),-1.0]])]});
            var Q1;
            Q1=sQuery(id+"F2.wireOp",EDGE,"E141");
            var Q2;
            Q2=sQuery(id+"F2.wireOp",EDGE,"E140");
            var Q3;
            Q3=sQuery(id+"F2.wireOp",EDGE,"E139");
            var Q4;
            Q4=sQuery(id+"F2.wireOp",EDGE,"E129");
            var Q5;
            Q5=sQuery(id+"F2.wireOp",EDGE,"E128");
            var Q6;
            Q6=sQuery(id+"F2.wireOp",EDGE,"E127");
            sweep(context, id + "F12", {"operationType" : NewBodyOperationType.REMOVE, "profiles" : qUnion([Q0]), "path" : qUnion([Q1, Q2, Q3, Q4, Q5, Q6])});
        }
        {
            var Q0;
            Q0=makeQuery(id+"F4.imprint","IMPRINT",FACE,{"disambiguationData":[TD([[makeQuery(id+"F4.imprint","IMPRINT",EDGE,{"derivedFrom":sQuery(id+"F4.wireOp",EDGE,"E161.rect.bottom")}),-1.0]])]});
            var Q1;
            Q1=sQuery(id+"F2.wireOp",EDGE,"E138");
            var Q2;
            Q2=sQuery(id+"F2.wireOp",EDGE,"E137");
            var Q3;
            Q3=sQuery(id+"F2.wireOp",EDGE,"E136");
            var Q4;
            Q4=sQuery(id+"F2.wireOp",EDGE,"E125");
            var Q5;
            Q5=sQuery(id+"F2.wireOp",EDGE,"E124");
            var Q6;
            Q6=sQuery(id+"F2.wireOp",EDGE,"E123");
            sweep(context, id + "F13", {"operationType" : NewBodyOperationType.REMOVE, "profiles" : qUnion([Q0]), "path" : qUnion([Q1, Q2, Q3, Q4, Q5, Q6])});
        }
        {
            var Q0;
            Q0=makeQuery(id+"F4.imprint","IMPRINT",FACE,{"disambiguationData":[TD([[makeQuery(id+"F4.imprint","IMPRINT",EDGE,{"derivedFrom":sQuery(id+"F4.wireOp",EDGE,"E162.rect.bottom")}),-1.0]])]});
            var Q1;
            Q1=sQuery(id+"F2.wireOp",EDGE,"E135");
            var Q2;
            Q2=sQuery(id+"F2.wireOp",EDGE,"E134");
            var Q3;
            Q3=sQuery(id+"F2.wireOp",EDGE,"E133");
            var Q4;
            Q4=sQuery(id+"F2.wireOp",EDGE,"E122");
            var Q5;
            Q5=sQuery(id+"F2.wireOp",EDGE,"E121");
            var Q6;
            Q6=sQuery(id+"F2.wireOp",EDGE,"E120");
            sweep(context, id + "F14", {"operationType" : NewBodyOperationType.REMOVE, "profiles" : qUnion([Q0]), "path" : qUnion([Q1, Q2, Q3, Q4, Q5, Q6])});
        }
        {
            var Q0;
            Q0=makeQuery(id+"F1.opExtrude","SWEPT_FACE",FACE,{"disambiguationData":[OSD([sQuery(id+"F0.wireOp",EDGE,"E0.rect.left")])]});
            var sketch = newSketch(context, id + "F15", { "sketchPlane" : qUnion([Q0])});
            skPoint(sketch, "E163.0", {"position": v(-95.25, 12.7) * mm});
            skPoint(sketch, "E164.0", {"position": v(-76.2, 12.7) * mm});
            skPoint(sketch, "E165.0", {"position": v(-57.15, 12.7) * mm});
            skPoint(sketch, "E166.0", {"position": v(-38.1, 12.7) * mm});
            skLineSegment(sketch, "E167", {"start": v(-133.35, 6.35) * mm, "end": v(-24.81, 6.35) * mm, "construction": true});
            skLineSegment(sketch, "E168.rect.bottom", {"start": v(-93.66, 6.35) * mm, "end": v(-96.84, 6.35) * mm});
            skLineSegment(sketch, "E168.rect.top", {"start": v(-93.66, 19.05) * mm, "end": v(-96.84, 19.05) * mm});
            skLineSegment(sketch, "E168.rect.left", {"start": v(-93.66, 6.35) * mm, "end": v(-93.66, 19.05) * mm});
            skLineSegment(sketch, "E168.rect.right", {"start": v(-96.84, 6.35) * mm, "end": v(-96.84, 19.05) * mm});
            skLineSegment(sketch, "E169.rect.bottom", {"start": v(-74.61, 6.35) * mm, "end": v(-77.79, 6.35) * mm});
            skLineSegment(sketch, "E169.rect.top", {"start": v(-74.61, 19.05) * mm, "end": v(-77.79, 19.05) * mm});
            skLineSegment(sketch, "E169.rect.left", {"start": v(-74.61, 6.35) * mm, "end": v(-74.61, 19.05) * mm});
            skLineSegment(sketch, "E169.rect.right", {"start": v(-77.79, 6.35) * mm, "end": v(-77.79, 19.05) * mm});
            skLineSegment(sketch, "E170.rect.bottom", {"start": v(-55.56, 6.35) * mm, "end": v(-58.74, 6.35) * mm});
            skLineSegment(sketch, "E170.rect.top", {"start": v(-55.56, 19.05) * mm, "end": v(-58.74, 19.05) * mm});
            skLineSegment(sketch, "E170.rect.left", {"start": v(-55.56, 6.35) * mm, "end": v(-55.56, 19.05) * mm});
            skLineSegment(sketch, "E170.rect.right", {"start": v(-58.74, 6.35) * mm, "end": v(-58.74, 19.05) * mm});
            skLineSegment(sketch, "E171.rect.bottom", {"start": v(-36.51, 6.35) * mm, "end": v(-39.69, 6.35) * mm});
            skLineSegment(sketch, "E171.rect.top", {"start": v(-36.51, 19.05) * mm, "end": v(-39.69, 19.05) * mm});
            skLineSegment(sketch, "E171.rect.left", {"start": v(-36.51, 6.35) * mm, "end": v(-36.51, 19.05) * mm});
            skLineSegment(sketch, "E171.rect.right", {"start": v(-39.69, 6.35) * mm, "end": v(-39.69, 19.05) * mm});
            skSolve(sketch);
        }
        {
            var Q0;
            {var subQ3=sQuery(id+"F15.wireOp",EDGE,"E168.rect.bottom");Q0=makeQuery(id+"F15.imprint","IMPRINT",FACE,{"disambiguationData":[TD([[makeQuery(id+"F15.imprint","IMPRINT",EDGE,{"derivedFrom":subQ3}),-1.0]])]});}
            var Q1;
            Q1=sQuery(id+"F2.wireOp",EDGE,"E32");
            var Q2;
            Q2=sQuery(id+"F2.wireOp",EDGE,"E34");
            var Q3;
            Q3=sQuery(id+"F2.wireOp",EDGE,"E33");
            sweep(context, id + "F16", {"operationType" : NewBodyOperationType.REMOVE, "profiles" : qUnion([Q0]), "path" : qUnion([Q1, Q2, Q3])});
        }
        {
            var Q0;
            {var subQ5=sQuery(id+"F15.wireOp",EDGE,"E169.rect.bottom");Q0=makeQuery(id+"F15.imprint","IMPRINT",FACE,{"disambiguationData":[TD([[makeQuery(id+"F15.imprint","IMPRINT",EDGE,{"derivedFrom":subQ5}),-1.0]])]});}
            var Q1;
            Q1=sQuery(id+"F2.wireOp",EDGE,"E35");
            var Q2;
            Q2=sQuery(id+"F2.wireOp",EDGE,"E36");
            var Q3;
            Q3=sQuery(id+"F2.wireOp",EDGE,"E37");
            sweep(context, id + "F17", {"operationType" : NewBodyOperationType.REMOVE, "profiles" : qUnion([Q0]), "path" : qUnion([Q1, Q2, Q3])});
        }
        {
            var Q0;
            {var subQ5=sQuery(id+"F15.wireOp",EDGE,"E170.rect.bottom");Q0=makeQuery(id+"F15.imprint","IMPRINT",FACE,{"disambiguationData":[TD([[makeQuery(id+"F15.imprint","IMPRINT",EDGE,{"derivedFrom":subQ5}),-1.0]])]});}
            var Q1;
            Q1=sQuery(id+"F2.wireOp",EDGE,"E38");
            var Q2;
            Q2=sQuery(id+"F2.wireOp",EDGE,"E39");
            var Q3;
            Q3=sQuery(id+"F2.wireOp",EDGE,"E40");
            sweep(context, id + "F18", {"operationType" : NewBodyOperationType.REMOVE, "profiles" : qUnion([Q0]), "path" : qUnion([Q1, Q2, Q3])});
        }
        {
            var Q0;
            {var subQ5=sQuery(id+"F15.wireOp",EDGE,"E171.rect.bottom");Q0=makeQuery(id+"F15.imprint","IMPRINT",FACE,{"disambiguationData":[TD([[makeQuery(id+"F15.imprint","IMPRINT",EDGE,{"derivedFrom":subQ5}),-1.0]])]});}
            var Q1;
            Q1=sQuery(id+"F2.wireOp",EDGE,"E41");
            var Q2;
            Q2=sQuery(id+"F2.wireOp",EDGE,"E42");
            var Q3;
            Q3=sQuery(id+"F2.wireOp",EDGE,"E43");
            sweep(context, id + "F19", {"operationType" : NewBodyOperationType.REMOVE, "profiles" : qUnion([Q0]), "path" : qUnion([Q1, Q2, Q3])});
        }
        {
            var Q0;
            Q0=qCreatedBy(makeId("Top.planeOp"),FACE);
            cPlane(context, id + "F20", {"entities" : qUnion([Q0]), "cplaneType" : CPlaneType.OFFSET, "offset" : 25.4 * mm, "width" : 152.4 * mm, "height" : 152.4 * mm});
        }
        {
            var Q0;
            Q0=qCreatedBy(id+"F20.planeOp",FACE);
            var sketch = newSketch(context, id + "F21", { "sketchPlane" : qUnion([Q0])});
            skLineSegment(sketch, "E172.bottom", {"start": v(-119.54, 96.78) * mm, "end": v(125.97, 96.78) * mm});
            skLineSegment(sketch, "E172.top", {"start": v(-119.54, 17.15) * mm, "end": v(125.97, 17.15) * mm});
            skLineSegment(sketch, "E172.left", {"start": v(-119.54, 96.78) * mm, "end": v(-119.54, 17.15) * mm});
            skLineSegment(sketch, "E172.right", {"start": v(125.97, 96.78) * mm, "end": v(125.97, 17.15) * mm});
            skSolve(sketch);
        }
        {
            var Q0;
            Q0=makeQuery(id+"F21.imprint","IMPRINT",FACE,{"disambiguationData":[TD([[makeQuery(id+"F21.imprint","IMPRINT",EDGE,{"derivedFrom":sQuery(id+"F21.wireOp",EDGE,"E172.bottom")}),-1.0]])]});
            extrude(context, id + "F22", {"entities" : qUnion([Q0]), "oppositeDirection" : true, "depth" : 6.35 * mm});
        }
        {
            var Q0;
            Q0=makeQuery(id+"F22.opExtrude","CAP_FACE",FACE,{"disambiguationData":[OSD([sQuery(id+"F21.wireOp",EDGE,"E172.bottom"),sQuery(id+"F21.wireOp",EDGE,"E172.top"),sQuery(id+"F21.wireOp",EDGE,"E172.left"),sQuery(id+"F21.wireOp",EDGE,"E172.right")])],"isStart":true});
            var sketch = newSketch(context, id + "F23", { "sketchPlane" : qUnion([Q0])});
            skLineSegment(sketch, "E173", {"start": v(-119.54, 37.7) * mm, "end": v(125.97, 37.7) * mm, "construction": true});
            skLineSegment(sketch, "E174", {"start": v(-119.54, 75.8) * mm, "end": v(125.97, 75.8) * mm, "construction": true});
            skLineSegment(sketch, "E175", {"start": v(-119.54, 56.75) * mm, "end": v(125.97, 56.75) * mm, "construction": true});
            skLineSegment(sketch, "E176.0", {"start": v(-60.96, 93.66) * mm, "end": v(-60.96, 58.74) * mm, "construction": true});
            skLineSegment(sketch, "E177.0", {"start": v(-60.96, 55.56) * mm, "end": v(-60.96, 39.69) * mm, "construction": true});
            skLineSegment(sketch, "E178.0", {"start": v(-60.96, 58.74) * mm, "end": v(-60.96, 55.56) * mm, "construction": true});
            skLineSegment(sketch, "E179.0", {"start": v(-60.96, 39.69) * mm, "end": v(-60.96, 36.51) * mm, "construction": true});
            skLineSegment(sketch, "E180.0", {"start": v(-60.96, 36.51) * mm, "end": v(-60.96, 30.34) * mm, "construction": true});
            skPoint(sketch, "E181", {"position": v(-60.96, 75.8) * mm});
            skPoint(sketch, "E182", {"position": v(-60.96, 37.7) * mm});
            skLineSegment(sketch, "E183", {"start": v(-54.61, 96.78) * mm, "end": v(-54.61, 17.15) * mm, "construction": true});
            skLineSegment(sketch, "E184", {"start": v(-54.61, 75.8) * mm, "end": v(-60.96, 75.8) * mm});
            skLineSegment(sketch, "E185", {"start": v(-60.96, 37.7) * mm, "end": v(-54.61, 37.7) * mm});
            skLineSegment(sketch, "E186", {"start": v(-54.61, 37.7) * mm, "end": v(-37.06, 56.75) * mm});
            skLineSegment(sketch, "E187", {"start": v(-37.06, 56.75) * mm, "end": v(-54.61, 75.8) * mm});
            skLineSegment(sketch, "E188", {"start": v(-37.06, 56.75) * mm, "end": v(23.5, 56.75) * mm});
            skLineSegment(sketch, "E189.0", {"start": v(60.96, 90.49) * mm, "end": v(60.96, 61.91) * mm, "construction": true});
            skLineSegment(sketch, "E190.0", {"start": v(60.96, 58.74) * mm, "end": v(60.96, 61.91) * mm, "construction": true});
            skLineSegment(sketch, "E191.0", {"start": v(60.96, 58.74) * mm, "end": v(60.96, 36.51) * mm, "construction": true});
            skLineSegment(sketch, "E192.0", {"start": v(60.96, 33.34) * mm, "end": v(60.96, 36.51) * mm, "construction": true});
            skLineSegment(sketch, "E193.0", {"start": v(60.96, 33.34) * mm, "end": v(60.96, 24.81) * mm, "construction": true});
            skLineSegment(sketch, "E194", {"start": v(64.13, 96.78) * mm, "end": v(64.13, 17.15) * mm, "construction": true});
            skLineSegment(sketch, "E195", {"start": v(57.78, 96.78) * mm, "end": v(57.78, 17.15) * mm, "construction": true});
            skLineSegment(sketch, "E196", {"start": v(64.13, 59.92) * mm, "end": v(57.78, 59.92) * mm, "construction": true});
            skLineSegment(sketch, "E197", {"start": v(57.78, 53.57) * mm, "end": v(64.13, 53.57) * mm, "construction": true});
            skLineSegment(sketch, "E198", {"start": v(64.13, 59.92) * mm, "end": v(110.1, 75.8) * mm});
            skLineSegment(sketch, "E199", {"start": v(110.1, 75.8) * mm, "end": v(125.97, 75.8) * mm});
            skLineSegment(sketch, "E200", {"start": v(110.1, 37.7) * mm, "end": v(64.13, 53.57) * mm});
            skLineSegment(sketch, "E201", {"start": v(110.1, 37.7) * mm, "end": v(125.97, 37.7) * mm});
            skLineSegment(sketch, "E202", {"start": v(57.78, 59.92) * mm, "end": v(64.13, 59.92) * mm});
            skLineSegment(sketch, "E203", {"start": v(64.13, 53.57) * mm, "end": v(57.78, 53.57) * mm});
            skLineSegment(sketch, "E204", {"start": v(-64.14, 96.78) * mm, "end": v(-64.14, 17.15) * mm, "construction": true});
            skLineSegment(sketch, "E205", {"start": v(-64.14, 75.8) * mm, "end": v(-60.96, 75.8) * mm});
            skLineSegment(sketch, "E206", {"start": v(-60.96, 37.7) * mm, "end": v(-64.14, 37.7) * mm});
            skLineSegment(sketch, "E207.0", {"start": v(-101.6, 77.79) * mm, "end": v(-101.6, 93.66) * mm, "construction": true});
            skLineSegment(sketch, "E208.0", {"start": v(-101.6, 74.61) * mm, "end": v(-101.6, 77.79) * mm, "construction": true});
            skLineSegment(sketch, "E209.0", {"start": v(-101.6, 58.74) * mm, "end": v(-101.6, 74.61) * mm, "construction": true});
            skLineSegment(sketch, "E210.0", {"start": v(-101.6, 55.56) * mm, "end": v(-101.6, 58.74) * mm, "construction": true});
            skLineSegment(sketch, "E211.0", {"start": v(-101.6, 39.69) * mm, "end": v(-101.6, 55.56) * mm, "construction": true});
            skLineSegment(sketch, "E212.0", {"start": v(-101.6, 36.51) * mm, "end": v(-101.6, 39.69) * mm, "construction": true});
            skLineSegment(sketch, "E213.0", {"start": v(-101.6, 24.81) * mm, "end": v(-101.6, 36.51) * mm, "construction": true});
            skLineSegment(sketch, "E214", {"start": v(-98.43, 96.78) * mm, "end": v(-98.43, 17.15) * mm, "construction": true});
            skLineSegment(sketch, "E215", {"start": v(-119.54, 75.8) * mm, "end": v(-101.6, 76.2) * mm});
            skLineSegment(sketch, "E216", {"start": v(-101.6, 76.2) * mm, "end": v(-98.43, 76.2) * mm});
            skLineSegment(sketch, "E217", {"start": v(-101.6, 57.15) * mm, "end": v(-98.43, 57.15) * mm});
            skLineSegment(sketch, "E218", {"start": v(-119.54, 37.7) * mm, "end": v(-101.6, 38.1) * mm});
            skLineSegment(sketch, "E219", {"start": v(-101.6, 38.1) * mm, "end": v(-98.43, 37.7) * mm});
            skLineSegment(sketch, "E220.bottom", {"start": v(-98.43, 81.48) * mm, "end": v(-64.14, 81.48) * mm});
            skLineSegment(sketch, "E220.top", {"start": v(-98.43, 31.92) * mm, "end": v(-64.14, 31.92) * mm});
            skLineSegment(sketch, "E220.left", {"start": v(-98.43, 81.48) * mm, "end": v(-98.43, 31.92) * mm});
            skLineSegment(sketch, "E220.right", {"start": v(-64.14, 81.48) * mm, "end": v(-64.14, 31.92) * mm});
            skLineSegment(sketch, "E221.0", {"start": v(20.32, -133.35) * mm, "end": v(20.32, 133.35) * mm, "construction": true});
            skLineSegment(sketch, "E222", {"start": v(23.5, 96.78) * mm, "end": v(23.5, 13.88) * mm, "construction": true});
            skLineSegment(sketch, "E223.bottom", {"start": v(23.5, 79.72) * mm, "end": v(60.96, 79.72) * mm});
            skLineSegment(sketch, "E223.top", {"start": v(23.5, 31.92) * mm, "end": v(60.96, 31.92) * mm});
            skLineSegment(sketch, "E223.left", {"start": v(23.5, 79.72) * mm, "end": v(23.5, 31.92) * mm});
            skLineSegment(sketch, "E223.right", {"start": v(60.96, 79.72) * mm, "end": v(60.96, 31.92) * mm});
            skSolve(sketch);
        }
        {
            var Q0;
            {var subQ7=sQuery(id+"F23.wireOp",EDGE,"E220.bottom");Q0=makeQuery(id+"F23.imprint","IMPRINT",FACE,{"disambiguationData":[TD([[makeQuery(id+"F23.imprint","IMPRINT",EDGE,{"derivedFrom":subQ7}),-1.0]])]});}
            var Q1;
            {var subQ4=sQuery(id+"F23.wireOp",EDGE,"E223.bottom");Q1=makeQuery(id+"F23.imprint","IMPRINT",FACE,{"disambiguationData":[TD([[makeQuery(id+"F23.imprint","IMPRINT",EDGE,{"derivedFrom":subQ4}),-1.0]])]});}
            var Q2;
            Q2=makeQuery(id+"F22.opExtrude","CAP_FACE",FACE,{"disambiguationData":[OSD([sQuery(id+"F21.wireOp",EDGE,"E172.bottom"),sQuery(id+"F21.wireOp",EDGE,"E172.top"),sQuery(id+"F21.wireOp",EDGE,"E172.left"),sQuery(id+"F21.wireOp",EDGE,"E172.right")])],"isStart":false});
            extrude(context, id + "F24", {"entities" : qUnion([Q0, Q1]), "operationType" : NewBodyOperationType.REMOVE, "endBound" : BoundingType.UP_TO_SURFACE, "oppositeDirection" : true, "endBoundEntityFace" : qUnion([Q2]), "depth" : 25.4 * mm});
        }
        {
            var Q0;
            Q0=makeQuery(id+"F22.opExtrude","SWEPT_FACE",FACE,{"disambiguationData":[OSD([sQuery(id+"F21.wireOp",EDGE,"E172.left")])]});
            var sketch = newSketch(context, id + "F25", { "sketchPlane" : qUnion([Q0])});
            skPoint(sketch, "E224", {"position": v(-75.81, 25.4) * mm});
            skPoint(sketch, "E225.0", {"position": v(-37.7, 25.4) * mm});
            skPoint(sketch, "E226.rect.cornerSnap0", {"position": v(-96.78, 22.22) * mm});
            skLineSegment(sketch, "E227.rect.bottom", {"start": v(-74.23, 18.29) * mm, "end": v(-77.4, 18.29) * mm});
            skLineSegment(sketch, "E227.rect.top", {"start": v(-74.23, 32.51) * mm, "end": v(-77.4, 32.51) * mm});
            skLineSegment(sketch, "E227.rect.left", {"start": v(-74.23, 18.29) * mm, "end": v(-74.23, 32.51) * mm});
            skLineSegment(sketch, "E227.rect.right", {"start": v(-77.4, 18.29) * mm, "end": v(-77.4, 32.51) * mm});
            skLineSegment(sketch, "E228.rect.bottom", {"start": v(-36.11, 16.82) * mm, "end": v(-39.29, 16.82) * mm});
            skLineSegment(sketch, "E228.rect.top", {"start": v(-36.11, 33.98) * mm, "end": v(-39.29, 33.98) * mm});
            skLineSegment(sketch, "E228.rect.left", {"start": v(-36.11, 16.82) * mm, "end": v(-36.11, 33.98) * mm});
            skLineSegment(sketch, "E228.rect.right", {"start": v(-39.29, 16.82) * mm, "end": v(-39.29, 33.98) * mm});
            skLineSegment(sketch, "E229", {"start": v(-96.78, 22.22) * mm, "end": v(-17.15, 22.22) * mm});
            skSolve(sketch);
        }
        {
            var Q0;
            {var subQ0=sQuery(id+"F21.wireOp",EDGE,"E172.left");var subQ4=sQuery(id+"F25.wireOp",EDGE,"E227.rect.left");var subQ6=makeQuery(id+"F22.opExtrude","CAP_EDGE",EDGE,{"disambiguationData":[OSD([subQ0])],"isStart":false});var subQ8=makeQuery(id+"F25.imprint","INTERSECT",VERTEX,{"derivedFrom":[subQ6,subQ4]});Q0=makeQuery(id+"F25.imprint","IMPRINT",FACE,{"disambiguationData":[TD([[makeQuery(id+"F25.imprint","IMPRINT",EDGE,{"disambiguationData":[TD([[subQ8,-1.0]])],"derivedFrom":subQ4}),1.0]])]});}
            var Q1;
            Q1=sQuery(id+"F23.wireOp",EDGE,"E215");
            var Q2;
            Q2=sQuery(id+"F23.wireOp",EDGE,"E216");
            sweep(context, id + "F26", {"operationType" : NewBodyOperationType.REMOVE, "profiles" : qUnion([Q0]), "path" : qUnion([Q1, Q2])});
        }
        {
            var Q0;
            {var subQ0=sQuery(id+"F21.wireOp",EDGE,"E172.left");var subQ1=makeQuery(id+"F22.opExtrude","CAP_EDGE",EDGE,{"disambiguationData":[OSD([subQ0])],"isStart":false});var subQ4=sQuery(id+"F25.wireOp",EDGE,"E228.rect.left");var subQ5=makeQuery(id+"F25.imprint","INTERSECT",VERTEX,{"derivedFrom":[subQ1,subQ4]});Q0=makeQuery(id+"F25.imprint","IMPRINT",FACE,{"disambiguationData":[TD([[makeQuery(id+"F25.imprint","IMPRINT",EDGE,{"disambiguationData":[TD([[subQ5,-1.0]])],"derivedFrom":subQ4}),1.0]])]});}
            var Q1;
            Q1=sQuery(id+"F23.wireOp",EDGE,"E218");
            var Q2;
            Q2=sQuery(id+"F23.wireOp",EDGE,"E219");
            sweep(context, id + "F27", {"operationType" : NewBodyOperationType.REMOVE, "profiles" : qUnion([Q0]), "path" : qUnion([Q1, Q2])});
        }
        {
            var Q0;
            Q0=makeQuery(id+"F24.boolean.opBoolean","COPY",FACE,{"derivedFrom":makeQuery(id+"F24.opExtrude","SWEPT_FACE",FACE,{"disambiguationData":[OSD([sQuery(id+"F23.wireOp",EDGE,"E220.right")])]})});
            var sketch = newSketch(context, id + "F28", { "sketchPlane" : qUnion([Q0])});
            skPoint(sketch, "E230.0", {"position": v(-75.8, 25.4) * mm});
            skPoint(sketch, "E231.0", {"position": v(-37.7, 25.4) * mm});
            skLineSegment(sketch, "E232.rect.bottom", {"start": v(-74.21, 17.7) * mm, "end": v(-77.39, 17.7) * mm});
            skLineSegment(sketch, "E232.rect.top", {"start": v(-74.21, 33.1) * mm, "end": v(-77.39, 33.1) * mm});
            skLineSegment(sketch, "E232.rect.left", {"start": v(-74.21, 17.7) * mm, "end": v(-74.21, 33.1) * mm});
            skLineSegment(sketch, "E232.rect.right", {"start": v(-77.39, 17.7) * mm, "end": v(-77.39, 33.1) * mm});
            skLineSegment(sketch, "E233.rect.bottom", {"start": v(-36.11, 17.85) * mm, "end": v(-39.29, 17.85) * mm});
            skLineSegment(sketch, "E233.rect.top", {"start": v(-36.11, 32.95) * mm, "end": v(-39.29, 32.95) * mm});
            skLineSegment(sketch, "E233.rect.left", {"start": v(-36.11, 17.85) * mm, "end": v(-36.11, 32.95) * mm});
            skLineSegment(sketch, "E233.rect.right", {"start": v(-39.29, 17.85) * mm, "end": v(-39.29, 32.95) * mm});
            skLineSegment(sketch, "E234", {"start": v(-81.48, 22.22) * mm, "end": v(-31.92, 22.22) * mm});
            skSolve(sketch);
        }
        {
            var Q0;
            {var subQ0=sQuery(id+"F23.wireOp",EDGE,"E220.right");var subQ1=makeQuery(id+"F24.boolean.opBoolean","COPY",EDGE,{"derivedFrom":makeQuery(id+"F24.opExtrude","CAP_EDGE",EDGE,{"disambiguationData":[OSD([subQ0])],"isStart":false})});var subQ4=sQuery(id+"F28.wireOp",EDGE,"E232.rect.left");var subQ5=makeQuery(id+"F28.imprint","INTERSECT",VERTEX,{"derivedFrom":[subQ1,subQ4]});Q0=makeQuery(id+"F28.imprint","IMPRINT",FACE,{"disambiguationData":[TD([[makeQuery(id+"F28.imprint","IMPRINT",EDGE,{"disambiguationData":[TD([[subQ5,-1.0]])],"derivedFrom":subQ4}),1.0]])]});}
            var Q1;
            Q1=sQuery(id+"F23.wireOp",EDGE,"E205");
            var Q2;
            Q2=sQuery(id+"F23.wireOp",EDGE,"E184");
            var Q3;
            Q3=sQuery(id+"F23.wireOp",EDGE,"E187");
            var Q4;
            Q4=sQuery(id+"F23.wireOp",EDGE,"E188");
            sweep(context, id + "F29", {"operationType" : NewBodyOperationType.REMOVE, "profiles" : qUnion([Q0]), "path" : qUnion([Q1, Q2, Q3, Q4])});
        }
        {
            var Q0;
            {var subQ0=sQuery(id+"F23.wireOp",EDGE,"E220.right");var subQ1=makeQuery(id+"F24.boolean.opBoolean","COPY",EDGE,{"derivedFrom":makeQuery(id+"F24.opExtrude","CAP_EDGE",EDGE,{"disambiguationData":[OSD([subQ0])],"isStart":false})});var subQ4=sQuery(id+"F28.wireOp",EDGE,"E233.rect.left");var subQ5=makeQuery(id+"F28.imprint","INTERSECT",VERTEX,{"derivedFrom":[subQ1,subQ4]});Q0=makeQuery(id+"F28.imprint","IMPRINT",FACE,{"disambiguationData":[TD([[makeQuery(id+"F28.imprint","IMPRINT",EDGE,{"disambiguationData":[TD([[subQ5,-1.0]])],"derivedFrom":subQ4}),1.0]])]});}
            var Q1;
            Q1=sQuery(id+"F23.wireOp",EDGE,"E206");
            var Q2;
            Q2=sQuery(id+"F23.wireOp",EDGE,"E185");
            var Q3;
            Q3=sQuery(id+"F23.wireOp",EDGE,"E186");
            sweep(context, id + "F30", {"operationType" : NewBodyOperationType.REMOVE, "profiles" : qUnion([Q0]), "path" : qUnion([Q1, Q2, Q3])});
        }
        {
            var Q0;
            Q0=makeQuery(id+"F22.opExtrude","SWEPT_FACE",FACE,{"disambiguationData":[OSD([sQuery(id+"F21.wireOp",EDGE,"E172.right")])]});
            var sketch = newSketch(context, id + "F31", { "sketchPlane" : qUnion([Q0])});
            skPoint(sketch, "E235.0", {"position": v(37.7, 25.4) * mm});
            skPoint(sketch, "E236.0", {"position": v(75.8, 25.4) * mm});
            skLineSegment(sketch, "E237.rect.bottom", {"start": v(39.29, 17.93) * mm, "end": v(36.11, 17.93) * mm});
            skLineSegment(sketch, "E237.rect.top", {"start": v(39.29, 32.87) * mm, "end": v(36.11, 32.87) * mm});
            skLineSegment(sketch, "E237.rect.left", {"start": v(39.29, 17.93) * mm, "end": v(39.29, 32.87) * mm});
            skLineSegment(sketch, "E237.rect.right", {"start": v(36.11, 17.93) * mm, "end": v(36.11, 32.87) * mm});
            skLineSegment(sketch, "E238.rect.bottom", {"start": v(77.39, 17.93) * mm, "end": v(74.21, 17.93) * mm});
            skLineSegment(sketch, "E238.rect.top", {"start": v(77.39, 32.87) * mm, "end": v(74.21, 32.87) * mm});
            skLineSegment(sketch, "E238.rect.left", {"start": v(77.39, 17.93) * mm, "end": v(77.39, 32.87) * mm});
            skLineSegment(sketch, "E238.rect.right", {"start": v(74.21, 17.93) * mm, "end": v(74.21, 32.87) * mm});
            skLineSegment(sketch, "E239", {"start": v(17.15, 22.22) * mm, "end": v(96.78, 22.22) * mm});
            skSolve(sketch);
        }
        {
            var Q0;
            {var subQ0=sQuery(id+"F21.wireOp",EDGE,"E172.right");var subQ1=makeQuery(id+"F22.opExtrude","CAP_EDGE",EDGE,{"disambiguationData":[OSD([subQ0])],"isStart":false});var subQ4=sQuery(id+"F31.wireOp",EDGE,"E237.rect.left");var subQ5=makeQuery(id+"F31.imprint","INTERSECT",VERTEX,{"derivedFrom":[subQ1,subQ4]});Q0=makeQuery(id+"F31.imprint","IMPRINT",FACE,{"disambiguationData":[TD([[makeQuery(id+"F31.imprint","IMPRINT",EDGE,{"disambiguationData":[TD([[subQ5,-1.0]])],"derivedFrom":subQ4}),1.0]])]});}
            var Q1;
            Q1=sQuery(id+"F23.wireOp",EDGE,"E201");
            var Q2;
            Q2=sQuery(id+"F23.wireOp",EDGE,"E200");
            var Q3;
            Q3=sQuery(id+"F23.wireOp",EDGE,"E203");
            sweep(context, id + "F32", {"operationType" : NewBodyOperationType.REMOVE, "profiles" : qUnion([Q0]), "path" : qUnion([Q1, Q2, Q3])});
        }
        {
            var Q0;
            {var subQ0=sQuery(id+"F21.wireOp",EDGE,"E172.right");var subQ1=makeQuery(id+"F22.opExtrude","CAP_EDGE",EDGE,{"disambiguationData":[OSD([subQ0])],"isStart":false});var subQ4=sQuery(id+"F31.wireOp",EDGE,"E238.rect.left");var subQ5=makeQuery(id+"F31.imprint","INTERSECT",VERTEX,{"derivedFrom":[subQ1,subQ4]});Q0=makeQuery(id+"F31.imprint","IMPRINT",FACE,{"disambiguationData":[TD([[makeQuery(id+"F31.imprint","IMPRINT",EDGE,{"disambiguationData":[TD([[subQ5,-1.0]])],"derivedFrom":subQ4}),1.0]])]});}
            var Q1;
            Q1=sQuery(id+"F23.wireOp",EDGE,"E199");
            var Q2;
            Q2=sQuery(id+"F23.wireOp",EDGE,"E198");
            var Q3;
            Q3=sQuery(id+"F23.wireOp",EDGE,"E202");
            sweep(context, id + "F33", {"operationType" : NewBodyOperationType.REMOVE, "profiles" : qUnion([Q0]), "path" : qUnion([Q1, Q2, Q3])});
        }
    });
